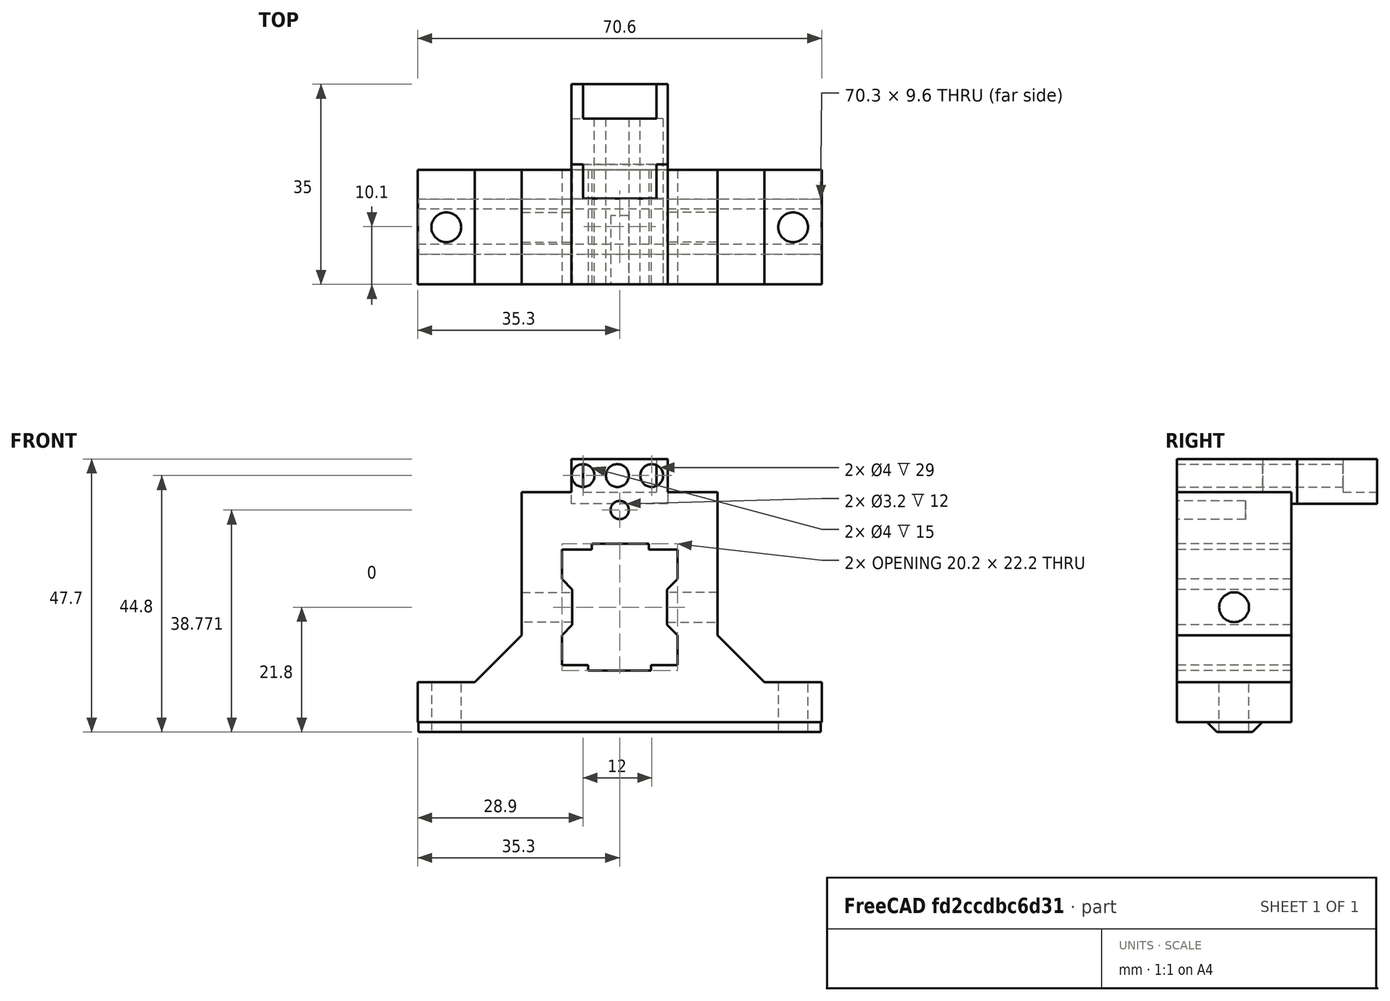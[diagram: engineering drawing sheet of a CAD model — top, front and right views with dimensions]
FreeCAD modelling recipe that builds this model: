
FCSTD DOCUMENT  (FreeCAD 1.0R39109 (Git))
Label: plotter_brace_limit_switch
License: All rights reserved
LicenseURL: https://en.wikipedia.org/wiki/All_rights_reserved
objects: Sketcher::SketchObject×24, PartDesign::Pocket×16, PartDesign::Pad×8, PartDesign::LinearPattern×2, PartDesign::Body×2, Mesh::Feature×1
note: 126 computed .brp shape members not serialized (recipe doc carries the construction recipe); baked Part::Feature solids carry a one-line shape summary decoded from their .brp

FEATURE [Mesh::Feature] _0x20_v_slot  label="20x20_v-slot"
FEATURE [Sketcher::SketchObject] Sketch
  ArcFitTolerance = 1e-06
  AttachmentSupport = -> [XZ_Plane]
  FullyConstrained = false
  MakeInternals = false
  MapMode = 5
  Placement = pos=(0,0,0) rot=(1,0,0;1.5708rad)
  sketch-geometry (28):
    g0: LineSegment StartX=-10.1 StartY=10.1 StartZ=0 EndX=-10.1 EndY=4.90001 EndZ=0
    g1: LineSegment StartX=-10.1 StartY=4.90001 StartZ=0 EndX=-8.3 EndY=3.09999 EndZ=0
    g2: LineSegment StartX=-8.3 StartY=3.09999 StartZ=0 EndX=-8.3 EndY=-3.10001 EndZ=0
    g3: LineSegment StartX=-8.3 StartY=-3.10001 StartZ=0 EndX=-10.1 EndY=-4.89999 EndZ=0
    g4: LineSegment StartX=-10.1 StartY=-4.89999 StartZ=0 EndX=-10.1 EndY=-10.1 EndZ=0
    g5: LineSegment StartX=-10.1 StartY=-10.1 StartZ=0 EndX=-5.47893 EndY=-10.1 EndZ=0
    g6: LineSegment StartX=-5.47893 StartY=-10.1 StartZ=0 EndX=-5.47893 EndY=-11.1 EndZ=0
    g7: LineSegment StartX=-5.47893 StartY=-11.1 StartZ=0 EndX=5.47893 EndY=-11.1 EndZ=0
    g8: LineSegment StartX=5.47893 StartY=-11.1 StartZ=0 EndX=5.47893 EndY=-10.1 EndZ=0
    g9: LineSegment StartX=5.47893 StartY=-10.1 StartZ=0 EndX=10.1 EndY=-10.1 EndZ=0
    g10: LineSegment StartX=10.1 StartY=-10.1 StartZ=0 EndX=10.1 EndY=-4.89999 EndZ=0
    g11: LineSegment StartX=10.1 StartY=-4.89999 StartZ=0 EndX=8.3 EndY=-3.09999 EndZ=0
    g12: LineSegment StartX=8.3 StartY=-3.09999 StartZ=0 EndX=8.3 EndY=3.10001 EndZ=0
    g13: LineSegment StartX=8.3 StartY=3.10001 StartZ=0 EndX=10.1 EndY=4.90001 EndZ=0
    g14: LineSegment StartX=10.1 StartY=4.90001 StartZ=0 EndX=10.1 EndY=10.1 EndZ=0
    g15: LineSegment StartX=17.1 StartY=10.1 StartZ=0 EndX=17.1 EndY=-4.89999 EndZ=0
    g16: LineSegment StartX=17.1 StartY=-4.89999 StartZ=0 EndX=25.3 EndY=-13.1 EndZ=0
    g17: LineSegment StartX=25.3 StartY=-13.1 StartZ=0 EndX=35.3 EndY=-13.1 EndZ=0
    g18: LineSegment StartX=35.3 StartY=-13.1 StartZ=0 EndX=35.3 EndY=-20.1 EndZ=0
    g19: LineSegment StartX=35.3 StartY=-20.1 StartZ=0 EndX=-35.3 EndY=-20.1 EndZ=0
    g20: LineSegment StartX=-35.3 StartY=-20.1 StartZ=0 EndX=-35.3 EndY=-13.1 EndZ=0
    g21: LineSegment StartX=-35.3 StartY=-13.1 StartZ=0 EndX=-25.3 EndY=-13.1 EndZ=0
    g22: LineSegment StartX=-25.3 StartY=-13.1 StartZ=0 EndX=-17.1 EndY=-4.89999 EndZ=0
    g23: LineSegment StartX=-17.1 StartY=-4.89999 StartZ=0 EndX=-17.1 EndY=10.1 EndZ=0
    g24: LineSegment StartX=-17.1 StartY=10.1 StartZ=0 EndX=-17.1 EndY=20.1 EndZ=0
    g25: LineSegment StartX=-17.1 StartY=20.1 StartZ=0 EndX=17.1 EndY=20.1 EndZ=0
    g26: LineSegment StartX=17.1 StartY=20.1 StartZ=0 EndX=17.1 EndY=10.1 EndZ=0
    g27: LineSegment StartX=10.1 StartY=10.1 StartZ=0 EndX=-10.1 EndY=10.1 EndZ=0
  constraints (81):
    c: Vertical(g0)
    c: Coincident(g0,g1)
    c: Coincident(g1,g2)
    c: Vertical(g2)
    c: Coincident(g2,g3)
    c: Coincident(g3,g4)
    c: Vertical(g4)
    c: Coincident(g4,g5)
    c: Horizontal(g5)
    c: Coincident(g5,g6)
    c: Vertical(g6)
    c: Coincident(g6,g7)
    c: Horizontal(g7)
    c: Coincident(g7,g8)
    c: Vertical(g8)
    c: Coincident(g8,g9)
    c: Horizontal(g9)
    c: Coincident(g9,g10)
    c: Vertical(g10)
    c: Coincident(g10,g11)
    c: Coincident(g11,g12)
    c: Vertical(g12)
    c: Coincident(g12,g13)
    c: Coincident(g13,g14)
    c: Vertical(g14)
    c: Vertical(g15)
    c: Coincident(g15,g16)
    c: Coincident(g16,g17)
    c: Horizontal(g17)
    c: Coincident(g17,g18)
    c: Vertical(g18)
    c: Coincident(g18,g19)
    c: Coincident(g19,g20)
    c: Vertical(g20)
    c: Coincident(g20,g21)
    c: Horizontal(g21)
    c: Coincident(g21,g22)
    c: Coincident(g22,g23)
    c: Vertical(g23)
    c: Equal(g15,g23)
    c: Equal(g14,g0)
    c: Equal(g12,g2)
    c: Equal(g4,g10)
    c: Equal(g9,g5)
    c: Equal(g6,g8)
    c: DistanceY(g8,g8) = 1
    c: DistanceY(g18,g18) = 7
    c: Equal(g20,g18)
    c: Equal(g21,g17)
    c: Symmetric(g18,g19,g-2)
    c: DistanceX(g4,g9) = 20.2
    c: DistanceX(g0,g14) = 20.2
    c: Perpendicular(g3,g1)
    c: Perpendicular(g11,g13)
    c: DistanceY(g2,g2) = 6.2
    c: DistanceX(g3,g2) = 1.8
    c: DistanceX(g11,g10) = 1.8
    c: DistanceY(g9,g14) = 20.2
    c: DistanceY(g14,g0) = 0
    c: DistanceX(g17,g17) = 10
    c: DistanceX(g14,g15) = 7
    c: Equal(g10,g14)
    c: Equal(g13,g11)
    c: Equal(g16,g22)
    c: Symmetric(g12,g2,g-1)
    c: DistanceY(g18,g9) = 10
    c: Perpendicular(g16,g22)
    c: DistanceY(g15,g10) = 0
    c: DistanceX(g23,g0) = 7
    c: Coincident(g23,g24)
    c: Vertical(g24)
    c: Coincident(g24,g25)
    c: Horizontal(g25)
    c: Coincident(g25,g26)
    c: Coincident(g26,g15)
    c: Vertical(g26)
    c: Coincident(g14,g27)
    c: Coincident(g27,g0)
    c: Equal(g24,g26)
    c: DistanceY(g26,g26) = 10
    c: DistanceY(g14,g15) = 0
FEATURE [PartDesign::Pad] Pad
  Direction = (0,-1,2e-16)
  Length = 20
  Length2 = 10
  Placement = pos=(0,0,0) rot=(1,0,0;1.5708rad)
  Profile = -> Sketch
  ReferenceAxis = -> Sketch [N_Axis]
  Refine = true
  Suppressed = false
  Type = 0
FEATURE [Sketcher::SketchObject] Sketch001
  ArcFitTolerance = 1e-06
  AttachmentSupport = -> [Pad]
  FullyConstrained = true
  MakeInternals = false
  MapMode = 5
  Placement = pos=(8.3,0,0) rot=(0.707107,0,-0.707107;3.14159rad)
  sketch-geometry (1):
    g0: Circle CenterX=0 CenterY=10 CenterZ=0 NormalX=0 NormalY=0 NormalZ=1 AngleXU=0 Radius=2.6
  constraints (4):
    c: Diameter(g0) = 5.2
    c: PointOnObject(g0,g-2)
    c: DistanceY(g-1,g0) = 10
    c: DistanceY(g-3,g-3) = 20
FEATURE [PartDesign::Pocket] Pocket
  BaseFeature = -> Pad
  Direction = (1,0,2e-16)
  Length = 100
  Length2 = 5
  Placement = pos=(0,0,0) rot=(1,0,0;1.5708rad)
  Profile = -> Sketch001
  ReferenceAxis = -> Sketch001 [N_Axis]
  Refine = true
  Suppressed = false
  Type = 0
FEATURE [PartDesign::Pocket] Pocket001
  BaseFeature = -> Pocket
  Direction = (1,0,2e-16)
  Length = 40
  Length2 = 5
  Placement = pos=(0,0,0) rot=(1,0,0;1.5708rad)
  Profile = -> Sketch001
  ReferenceAxis = -> Sketch001 [N_Axis]
  Refine = true
  Reversed = true
  Suppressed = false
  Type = 0
FEATURE [Sketcher::SketchObject] Sketch002
  ArcFitTolerance = 1e-06
  FullyConstrained = true
  MakeInternals = false
  MapMode = 5
  Placement = pos=(0,-20,0) rot=(1,0,0;1.5708rad)
  sketch-geometry (4):
    g0: LineSegment StartX=-10.05 StartY=4.89999 StartZ=0 EndX=-10.05 EndY=-4.90001 EndZ=0
    g1: LineSegment StartX=-10.05 StartY=-4.90001 StartZ=0 EndX=-8.25 EndY=-3.09999 EndZ=0
    g2: LineSegment StartX=-8.25 StartY=-3.09999 StartZ=0 EndX=-8.25 EndY=3.10001 EndZ=0
    g3: LineSegment StartX=-8.25 StartY=3.10001 StartZ=0 EndX=-10.05 EndY=4.89999 EndZ=0
  constraints (8):
    c: Coincident(g-3,g0)
    c: Coincident(g0,g-5)
    c: Coincident(g0,g1)
    c: Coincident(g1,g-5)
    c: Coincident(g1,g2)
    c: Coincident(g2,g-4)
    c: Coincident(g2,g3)
    c: Coincident(g3,g0)
FEATURE [Sketcher::SketchObject] Sketch003
  ArcFitTolerance = 1e-06
  FullyConstrained = true
  MakeInternals = false
  MapMode = 5
  Placement = pos=(35.15,0,0) rot=(0.707107,0,0.707107;3.14159rad)
  sketch-geometry (5):
    g0: GeomPoint X=-20 Y=10 Z=0
    g1: LineSegment StartX=-20 StartY=14.8 StartZ=0 EndX=-20 EndY=5 EndZ=0
    g2: LineSegment StartX=-20 StartY=5 StartZ=0 EndX=-21.8 EndY=6.8 EndZ=0
    g3: LineSegment StartX=-21.8 StartY=6.8 StartZ=0 EndX=-21.8 EndY=13 EndZ=0
    g4: LineSegment StartX=-21.8 StartY=13 StartZ=0 EndX=-20 EndY=14.8 EndZ=0
  constraints (12):
    c: Symmetric(g-3,g-3,g0)
    c: Coincident(g1,g2)
    c: Coincident(g2,g3)
    c: Coincident(g3,g4)
    c: Coincident(g4,g1)
    c: Equal(g2,g4)
    c: Parallel(g1,g3)
    c: DistanceY(g3,g3) = 6.2
    c: DistanceY(g1,g1) = 9.8
    c: Perpendicular(g4,g2)
    c: PointOnObject(g1,g-3)
    c: Symmetric(g0,g-3,g1)
FEATURE [PartDesign::Pad] Pad001
  BaseFeature = -> Pocket001
  Direction = (1,-1e-16,-2e-16)
  Length = 70.3
  Length2 = 10
  Placement = pos=(0,0,0) rot=(1,0,0;1.5708rad)
  Profile = -> Sketch003
  ReferenceAxis = -> Sketch003 [N_Axis]
  Refine = true
  Reversed = true
  Suppressed = false
  Type = 0
FEATURE [Sketcher::SketchObject] Sketch004
  ArcFitTolerance = 1e-06
  AttachmentSupport = -> [Pad001]
  ExternalGeometry = -> [Pad001]
  FullyConstrained = true
  MakeInternals = false
  MapMode = 5
  Placement = pos=(0,-2.9e-15,-13.1) rot=(0,0,1;3.14159rad)
  sketch-geometry (1):
    g0: Circle CenterX=-30.3 CenterY=10 CenterZ=0 NormalX=0 NormalY=0 NormalZ=1 AngleXU=0 Radius=2.6
  constraints (2):
    c: Diameter(g0) = 5.2
    c: Symmetric(g-4,g-3,g0)
FEATURE [PartDesign::Pocket] Pocket002
  BaseFeature = -> Pad001
  Direction = (0,0,-1)
  Length = 10
  Length2 = 5
  Placement = pos=(0,0,0) rot=(1,0,0;1.5708rad)
  Profile = -> Sketch004
  ReferenceAxis = -> Sketch004 [N_Axis]
  Refine = true
  Suppressed = false
  Type = 0
FEATURE [Sketcher::SketchObject] Sketch005
  ArcFitTolerance = 1e-06
  AttachmentSupport = -> [Pocket002]
  ExternalGeometry = -> [Pocket002]
  FullyConstrained = true
  MakeInternals = false
  MapMode = 5
  Placement = pos=(0,-2.9e-15,-13.1) rot=(0,0,1;3.14159rad)
  sketch-geometry (1):
    g0: Circle CenterX=30.3 CenterY=10 CenterZ=0 NormalX=0 NormalY=0 NormalZ=1 AngleXU=0 Radius=2.6
  constraints (2):
    c: Diameter(g0) = 5.2
    c: Symmetric(g-4,g-3,g0)
FEATURE [PartDesign::Pocket] Pocket003
  BaseFeature = -> Pocket002
  Direction = (0,0,-1)
  Length = 10
  Length2 = 5
  Placement = pos=(0,0,0) rot=(1,0,0;1.5708rad)
  Profile = -> Sketch005
  ReferenceAxis = -> Sketch005 [N_Axis]
  Refine = true
  Suppressed = false
  Type = 0
FEATURE [Sketcher::SketchObject] Sketch006
  ArcFitTolerance = 1e-06
  AttachmentSupport = -> [Pocket003]
  ExternalGeometry = -> [Pocket003]
  FullyConstrained = true
  MakeInternals = false
  MapMode = 5
  Placement = pos=(0,-8e-16,0) rot=(-1,0,0;1.5708rad)
  sketch-geometry (4):
    g0: LineSegment StartX=-4.9 StartY=-10.1 StartZ=0 EndX=-4.9 EndY=-11.1 EndZ=0
    g1: LineSegment StartX=-4.9 StartY=-11.1 StartZ=0 EndX=5.1 EndY=-11.1 EndZ=0
    g2: LineSegment StartX=5.1 StartY=-11.1 StartZ=0 EndX=5.1 EndY=-10.1 EndZ=0
    g3: LineSegment StartX=5.1 StartY=-10.1 StartZ=0 EndX=-4.9 EndY=-10.1 EndZ=0
  constraints (12):
    c: Coincident(g0,g1)
    c: Coincident(g1,g2)
    c: Coincident(g2,g3)
    c: Coincident(g3,g0)
    c: Vertical(g0)
    c: Vertical(g2)
    c: Horizontal(g1)
    c: Horizontal(g3)
    c: Distance(g0,g2) = 10
    c: Distance(g1,g3) = 1
    c: PointOnObject(g0,g-3)
    c: DistanceX(g2,g-3) = 5
FEATURE [PartDesign::Pocket] Pocket004
  BaseFeature = -> Pocket003
  Direction = (0,-1,-2e-16)
  Length = 25
  Length2 = 5
  Placement = pos=(0,0,0) rot=(1,0,0;1.5708rad)
  Profile = -> Sketch006
  ReferenceAxis = -> Sketch006 [N_Axis]
  Refine = true
  Suppressed = false
  Type = 0
FEATURE [Sketcher::SketchObject] Sketch007
  ArcFitTolerance = 1e-06
  AttachmentSupport = -> [Pocket004]
  ExternalGeometry = -> [Pocket004]
  FullyConstrained = false
  MakeInternals = false
  MapMode = 5
  Placement = pos=(0,4.5e-15,20.1) rot=(0,0,1;3.14159rad)
  sketch-geometry (7):
    g0: GeomPoint X=0 Y=20 Z=0
    g1: GeomPoint X=0 Y=0 Z=0
    g2: LineSegment StartX=-8.4 StartY=-15 StartZ=0 EndX=8.4 EndY=-15 EndZ=0
    g3: LineSegment StartX=8.4 StartY=-15 StartZ=0 EndX=8.4 EndY=20 EndZ=0
    g4: LineSegment StartX=8.4 StartY=20 StartZ=0 EndX=-8.4 EndY=20 EndZ=0
    g5: LineSegment StartX=-8.4 StartY=20 StartZ=0 EndX=-8.4 EndY=-15 EndZ=0
    g6: GeomPoint [constr] X=0 Y=2.5 Z=0
  constraints (14):
    c: Symmetric(g-3,g-3,g0)
    c: Coincident(g2,g3)
    c: Coincident(g3,g4)
    c: Coincident(g4,g5)
    c: Coincident(g5,g2)
    c: Horizontal(g2)
    c: Horizontal(g4)
    c: Vertical(g3)
    c: Vertical(g5)
    c: Symmetric(g4,g2,g6)
    c: Distance(g3,g5) = 16.8
    c: Distance(g2,g4) = 35
    c: PointOnObject(g6,g-2)
    c: PointOnObject(g3,g-3)
FEATURE [PartDesign::Pad] Pad002
  BaseFeature = -> Pocket004
  Direction = (0,0,1)
  Length = 5.8
  Length2 = 10
  Placement = pos=(0,0,0) rot=(1,0,0;1.5708rad)
  Profile = -> Sketch007
  ReferenceAxis = -> Sketch007 [N_Axis]
  Refine = true
  Suppressed = false
  Type = 0
FEATURE [Sketcher::SketchObject] Sketch008
  ArcFitTolerance = 1e-06
  AttachmentSupport = -> [Pad002]
  ExternalGeometry = -> [Pad002]
  FullyConstrained = true
  MakeInternals = false
  MapMode = 5
  Placement = pos=(0,0,25.9) rot=(0,0,1;3.14159rad)
  sketch-geometry (6):
    g0: LineSegment [constr] StartX=-8.4 StartY=-15 StartZ=0 EndX=-6.4 EndY=-15 EndZ=0
    g1: LineSegment StartX=-6.4 StartY=-15 StartZ=0 EndX=-6.4 EndY=-9 EndZ=0
    g2: LineSegment StartX=-6.4 StartY=-9 StartZ=0 EndX=6.4 EndY=-9 EndZ=0
    g3: LineSegment StartX=6.4 StartY=-9 StartZ=0 EndX=6.4 EndY=-15 EndZ=0
    g4: LineSegment [constr] StartX=6.4 StartY=-15 StartZ=0 EndX=8.4 EndY=-15 EndZ=0
    g5: LineSegment StartX=-6.4 StartY=-15 StartZ=0 EndX=6.4 EndY=-15 EndZ=0
  constraints (16):
    c: Coincident(g-3,g0)
    c: PointOnObject(g0,g-3)
    c: Coincident(g0,g1)
    c: Vertical(g1)
    c: Coincident(g1,g2)
    c: Horizontal(g2)
    c: Coincident(g2,g3)
    c: PointOnObject(g3,g-3)
    c: Vertical(g3)
    c: Coincident(g3,g4)
    c: Coincident(g4,g-3)
    c: Equal(g4,g0)
    c: DistanceX(g0,g0) = 2
    c: DistanceY(g3,g3) = 6
    c: Coincident(g5,g0)
    c: Coincident(g5,g3)
FEATURE [PartDesign::Pocket] Pocket005
  BaseFeature = -> Pad002
  Direction = (0,0,-1)
  Length = 5.8
  Length2 = 5
  Placement = pos=(0,0,0) rot=(1,0,0;1.5708rad)
  Profile = -> Sketch008
  ReferenceAxis = -> Sketch008 [N_Axis]
  Refine = true
  Suppressed = false
  Type = 0
FEATURE [Sketcher::SketchObject] Sketch009
  ArcFitTolerance = 1e-06
  AttachmentSupport = -> [Pocket005]
  ExternalGeometry = -> [Pocket005]
  FullyConstrained = true
  MakeInternals = false
  MapMode = 5
  Placement = pos=(0,-8e-16,0) rot=(-1,0,0;1.5708rad)
  sketch-geometry (4):
    g0: LineSegment StartX=-8.4 StartY=-20.1 StartZ=0 EndX=8.4 EndY=-20.1 EndZ=0
    g1: LineSegment StartX=8.4 StartY=-20.1 StartZ=0 EndX=8.4 EndY=-18.1 EndZ=0
    g2: LineSegment StartX=8.4 StartY=-18.1 StartZ=0 EndX=-8.4 EndY=-18.1 EndZ=0
    g3: LineSegment StartX=-8.4 StartY=-18.1 StartZ=0 EndX=-8.4 EndY=-20.1 EndZ=0
  constraints (11):
    c: Coincident(g0,g1)
    c: Coincident(g1,g2)
    c: Coincident(g2,g3)
    c: Coincident(g3,g0)
    c: Horizontal(g0)
    c: Horizontal(g2)
    c: Vertical(g1)
    c: Vertical(g3)
    c: Distance(g1,g3) = 16.8
    c: Distance(g0,g2) = 2
    c: Coincident(g0,g-3)
FEATURE [PartDesign::Pad] Pad003
  BaseFeature = -> Pocket005
  Direction = (0,1,2e-16)
  Length = 15
  Length2 = 10
  Placement = pos=(0,0,0) rot=(1,0,0;1.5708rad)
  Profile = -> Sketch009
  ReferenceAxis = -> Sketch009 [N_Axis]
  Refine = true
  Suppressed = false
  Type = 0
FEATURE [Sketcher::SketchObject] Sketch010
  ArcFitTolerance = 1e-06
  AttachmentSupport = -> [Pad003]
  ExternalGeometry = -> [Pad003]
  FullyConstrained = true
  MakeInternals = false
  MapMode = 5
  Placement = pos=(0,9,0) rot=(-1,0,0;1.5708rad)
  sketch-geometry (1):
    g0: Circle CenterX=-6.4 CenterY=-23 CenterZ=0 NormalX=0 NormalY=0 NormalZ=1 AngleXU=0 Radius=2
  constraints (2):
    c: Diameter(g0) = 4
    c: Symmetric(g-5,g-5,g0)
FEATURE [PartDesign::Pocket] Pocket006
  BaseFeature = -> Pad003
  Direction = (0,-1,-2e-16)
  Length = 40
  Length2 = 5
  Placement = pos=(0,0,0) rot=(1,0,0;1.5708rad)
  Profile = -> Sketch010
  ReferenceAxis = -> Sketch010 [N_Axis]
  Refine = true
  Suppressed = false
  Type = 0
FEATURE [PartDesign::LinearPattern] LinearPattern
  BaseFeature = -> Pocket006
  Direction = -> Sketch010 [H_Axis]
  Length = 12
  Mode = 0
  Occurrences = 3
  Offset = 6
  Originals = -> [Pocket006]
  Placement = pos=(0,0,0) rot=(1,0,0;1.5708rad)
  Refine = true
  Suppressed = false
  TransformMode = 0
FEATURE [Sketcher::SketchObject] Sketch011
  ArcFitTolerance = 1e-06
  AttachmentSupport = -> [LinearPattern]
  FullyConstrained = false
  MakeInternals = false
  MapMode = 5
  Placement = pos=(0,-20,4.4e-15) rot=(1,0,0;1.5708rad)
  sketch-geometry (1):
    g0: Circle CenterX=0 CenterY=16.9706 CenterZ=0 NormalX=0 NormalY=0 NormalZ=1 AngleXU=0 Radius=1.6
  constraints (2):
    c: Diameter(g0) = 3.2
    c: PointOnObject(g0,g-2)
FEATURE [PartDesign::Pocket] Pocket007
  BaseFeature = -> LinearPattern
  Direction = (0,1,-2e-16)
  Length = 12
  Length2 = 5
  Placement = pos=(0,0,0) rot=(1,0,0;1.5708rad)
  Profile = -> Sketch011
  ReferenceAxis = -> Sketch011 [N_Axis]
  Refine = true
  Suppressed = false
  Type = 0
FEATURE [PartDesign::Body] Body  label="main"
  AllowCompound = false
  Group = -> [Sketch,Pad,Sketch001,Pocket,Pocket001,Sketch002,Sketch003,Pad001,Sketch004,Pocket002,Sketch005,Pocket003,Sketch006,Pocket004,Sketch007,Pad002,Sketch008,Pocket005,Sketch009,Pad003,Sketch010,Pocket006,LinearPattern,Sketch011,Pocket007]
  Origin = -> Origin
  Tip = -> Pocket007
FEATURE [Sketcher::SketchObject] Sketch012
  ArcFitTolerance = 1e-06
  AttachmentSupport = -> [XZ_Plane001]
  FullyConstrained = false
  MakeInternals = false
  MapMode = 5
  Placement = pos=(0,0,0) rot=(1,0,0;1.5708rad)
  sketch-geometry (28):
    g0: LineSegment StartX=-10.1 StartY=10.1 StartZ=0 EndX=-10.1 EndY=4.90001 EndZ=0
    g1: LineSegment StartX=-10.1 StartY=4.90001 StartZ=0 EndX=-8.3 EndY=3.09999 EndZ=0
    g2: LineSegment StartX=-8.3 StartY=3.09999 StartZ=0 EndX=-8.3 EndY=-3.10001 EndZ=0
    g3: LineSegment StartX=-8.3 StartY=-3.10001 StartZ=0 EndX=-10.1 EndY=-4.89999 EndZ=0
    g4: LineSegment StartX=-10.1 StartY=-4.89999 StartZ=0 EndX=-10.1 EndY=-10.1 EndZ=0
    g5: LineSegment StartX=-10.1 StartY=-10.1 StartZ=0 EndX=-5.47893 EndY=-10.1 EndZ=0
    g6: LineSegment StartX=-5.47893 StartY=-10.1 StartZ=0 EndX=-5.47893 EndY=-11.1 EndZ=0
    g7: LineSegment StartX=-5.47893 StartY=-11.1 StartZ=0 EndX=5.47893 EndY=-11.1 EndZ=0
    g8: LineSegment StartX=5.47893 StartY=-11.1 StartZ=0 EndX=5.47893 EndY=-10.1 EndZ=0
    g9: LineSegment StartX=5.47893 StartY=-10.1 StartZ=0 EndX=10.1 EndY=-10.1 EndZ=0
    g10: LineSegment StartX=10.1 StartY=-10.1 StartZ=0 EndX=10.1 EndY=-4.89999 EndZ=0
    g11: LineSegment StartX=10.1 StartY=-4.89999 StartZ=0 EndX=8.3 EndY=-3.09999 EndZ=0
    g12: LineSegment StartX=8.3 StartY=-3.09999 StartZ=0 EndX=8.3 EndY=3.10001 EndZ=0
    g13: LineSegment StartX=8.3 StartY=3.10001 StartZ=0 EndX=10.1 EndY=4.90001 EndZ=0
    g14: LineSegment StartX=10.1 StartY=4.90001 StartZ=0 EndX=10.1 EndY=10.1 EndZ=0
    g15: LineSegment StartX=17.1 StartY=10.1 StartZ=0 EndX=17.1 EndY=-4.89999 EndZ=0
    g16: LineSegment StartX=17.1 StartY=-4.89999 StartZ=0 EndX=25.3 EndY=-13.1 EndZ=0
    g17: LineSegment StartX=25.3 StartY=-13.1 StartZ=0 EndX=35.3 EndY=-13.1 EndZ=0
    g18: LineSegment StartX=35.3 StartY=-13.1 StartZ=0 EndX=35.3 EndY=-20.1 EndZ=0
    g19: LineSegment StartX=35.3 StartY=-20.1 StartZ=0 EndX=-35.3 EndY=-20.1 EndZ=0
    g20: LineSegment StartX=-35.3 StartY=-20.1 StartZ=0 EndX=-35.3 EndY=-13.1 EndZ=0
    g21: LineSegment StartX=-35.3 StartY=-13.1 StartZ=0 EndX=-25.3 EndY=-13.1 EndZ=0
    g22: LineSegment StartX=-25.3 StartY=-13.1 StartZ=0 EndX=-17.1 EndY=-4.89999 EndZ=0
    g23: LineSegment StartX=-17.1 StartY=-4.89999 StartZ=0 EndX=-17.1 EndY=10.1 EndZ=0
    g24: LineSegment StartX=-17.1 StartY=10.1 StartZ=0 EndX=-17.1 EndY=20.1 EndZ=0
    g25: LineSegment StartX=-17.1 StartY=20.1 StartZ=0 EndX=17.1 EndY=20.1 EndZ=0
    g26: LineSegment StartX=17.1 StartY=20.1 StartZ=0 EndX=17.1 EndY=10.1 EndZ=0
    g27: LineSegment StartX=10.1 StartY=10.1 StartZ=0 EndX=-10.1 EndY=10.1 EndZ=0
  constraints (81):
    c: Vertical(g0)
    c: Coincident(g0,g1)
    c: Coincident(g1,g2)
    c: Vertical(g2)
    c: Coincident(g2,g3)
    c: Coincident(g3,g4)
    c: Vertical(g4)
    c: Coincident(g4,g5)
    c: Horizontal(g5)
    c: Coincident(g5,g6)
    c: Vertical(g6)
    c: Coincident(g6,g7)
    c: Horizontal(g7)
    c: Coincident(g7,g8)
    c: Vertical(g8)
    c: Coincident(g8,g9)
    c: Horizontal(g9)
    c: Coincident(g9,g10)
    c: Vertical(g10)
    c: Coincident(g10,g11)
    c: Coincident(g11,g12)
    c: Vertical(g12)
    c: Coincident(g12,g13)
    c: Coincident(g13,g14)
    c: Vertical(g14)
    c: Vertical(g15)
    c: Coincident(g15,g16)
    c: Coincident(g16,g17)
    c: Horizontal(g17)
    c: Coincident(g17,g18)
    c: Vertical(g18)
    c: Coincident(g18,g19)
    c: Coincident(g19,g20)
    c: Vertical(g20)
    c: Coincident(g20,g21)
    c: Horizontal(g21)
    c: Coincident(g21,g22)
    c: Coincident(g22,g23)
    c: Vertical(g23)
    c: Equal(g15,g23)
    c: Equal(g14,g0)
    c: Equal(g12,g2)
    c: Equal(g4,g10)
    c: Equal(g9,g5)
    c: Equal(g6,g8)
    c: DistanceY(g8,g8) = 1
    c: DistanceY(g18,g18) = 7
    c: Equal(g20,g18)
    c: Equal(g21,g17)
    c: Symmetric(g18,g19,g-2)
    c: DistanceX(g4,g9) = 20.2
    c: DistanceX(g0,g14) = 20.2
    c: Perpendicular(g3,g1)
    c: Perpendicular(g11,g13)
    c: DistanceY(g2,g2) = 6.2
    c: DistanceX(g3,g2) = 1.8
    c: DistanceX(g11,g10) = 1.8
    c: DistanceY(g9,g14) = 20.2
    c: DistanceY(g14,g0) = 0
    c: DistanceX(g17,g17) = 10
    c: DistanceX(g14,g15) = 7
    c: Equal(g10,g14)
    c: Equal(g13,g11)
    c: Equal(g16,g22)
    c: Symmetric(g12,g2,g-1)
    c: DistanceY(g18,g9) = 10
    c: Perpendicular(g16,g22)
    c: DistanceY(g15,g10) = 0
    c: DistanceX(g23,g0) = 7
    c: Coincident(g23,g24)
    c: Vertical(g24)
    c: Coincident(g24,g25)
    c: Horizontal(g25)
    c: Coincident(g25,g26)
    c: Coincident(g26,g15)
    c: Vertical(g26)
    c: Coincident(g14,g27)
    c: Coincident(g27,g0)
    c: Equal(g24,g26)
    c: DistanceY(g26,g26) = 10
    c: DistanceY(g14,g15) = 0
FEATURE [PartDesign::Pad] Pad004
  Direction = (0,-1,2e-16)
  Length = 20
  Length2 = 10
  Placement = pos=(0,0,0) rot=(1,0,0;1.5708rad)
  Profile = -> Sketch012
  ReferenceAxis = -> Sketch012 [N_Axis]
  Refine = true
  Suppressed = false
  Type = 0
FEATURE [Sketcher::SketchObject] Sketch013
  ArcFitTolerance = 1e-06
  AttachmentSupport = -> [Pad004]
  FullyConstrained = true
  MakeInternals = false
  MapMode = 5
  Placement = pos=(8.3,0,0) rot=(0.707107,0,-0.707107;3.14159rad)
  sketch-geometry (1):
    g0: Circle CenterX=0 CenterY=10 CenterZ=0 NormalX=0 NormalY=0 NormalZ=1 AngleXU=0 Radius=2.6
  constraints (4):
    c: Diameter(g0) = 5.2
    c: PointOnObject(g0,g-2)
    c: DistanceY(g-1,g0) = 10
    c: DistanceY(g-3,g-3) = 20
FEATURE [PartDesign::Pocket] Pocket008
  BaseFeature = -> Pad004
  Direction = (1,0,2e-16)
  Length = 100
  Length2 = 5
  Placement = pos=(0,0,0) rot=(1,0,0;1.5708rad)
  Profile = -> Sketch013
  ReferenceAxis = -> Sketch013 [N_Axis]
  Refine = true
  Suppressed = false
  Type = 0
FEATURE [PartDesign::Pocket] Pocket009
  BaseFeature = -> Pocket008
  Direction = (1,0,2e-16)
  Length = 40
  Length2 = 5
  Placement = pos=(0,0,0) rot=(1,0,0;1.5708rad)
  Profile = -> Sketch013
  ReferenceAxis = -> Sketch013 [N_Axis]
  Refine = true
  Reversed = true
  Suppressed = false
  Type = 0
FEATURE [Sketcher::SketchObject] Sketch014
  ArcFitTolerance = 1e-06
  FullyConstrained = true
  MakeInternals = false
  MapMode = 5
  Placement = pos=(0,-20,0) rot=(1,0,0;1.5708rad)
  sketch-geometry (4):
    g0: LineSegment StartX=-10.05 StartY=4.89999 StartZ=0 EndX=-10.05 EndY=-4.90001 EndZ=0
    g1: LineSegment StartX=-10.05 StartY=-4.90001 StartZ=0 EndX=-8.25 EndY=-3.09999 EndZ=0
    g2: LineSegment StartX=-8.25 StartY=-3.09999 StartZ=0 EndX=-8.25 EndY=3.10001 EndZ=0
    g3: LineSegment StartX=-8.25 StartY=3.10001 StartZ=0 EndX=-10.05 EndY=4.89999 EndZ=0
  constraints (8):
    c: Coincident(g-3,g0)
    c: Coincident(g0,g-5)
    c: Coincident(g0,g1)
    c: Coincident(g1,g-5)
    c: Coincident(g1,g2)
    c: Coincident(g2,g-4)
    c: Coincident(g2,g3)
    c: Coincident(g3,g0)
FEATURE [Sketcher::SketchObject] Sketch015
  ArcFitTolerance = 1e-06
  FullyConstrained = true
  MakeInternals = false
  MapMode = 5
  Placement = pos=(35.15,0,0) rot=(0.707107,0,0.707107;3.14159rad)
  sketch-geometry (5):
    g0: GeomPoint X=-20 Y=10 Z=0
    g1: LineSegment StartX=-20 StartY=14.8 StartZ=0 EndX=-20 EndY=5 EndZ=0
    g2: LineSegment StartX=-20 StartY=5 StartZ=0 EndX=-21.8 EndY=6.8 EndZ=0
    g3: LineSegment StartX=-21.8 StartY=6.8 StartZ=0 EndX=-21.8 EndY=13 EndZ=0
    g4: LineSegment StartX=-21.8 StartY=13 StartZ=0 EndX=-20 EndY=14.8 EndZ=0
  constraints (12):
    c: Symmetric(g-3,g-3,g0)
    c: Coincident(g1,g2)
    c: Coincident(g2,g3)
    c: Coincident(g3,g4)
    c: Coincident(g4,g1)
    c: Equal(g2,g4)
    c: Parallel(g1,g3)
    c: DistanceY(g3,g3) = 6.2
    c: DistanceY(g1,g1) = 9.8
    c: Perpendicular(g4,g2)
    c: PointOnObject(g1,g-3)
    c: Symmetric(g0,g-3,g1)
FEATURE [PartDesign::Pad] Pad005
  BaseFeature = -> Pocket009
  Direction = (1,-1e-16,-2e-16)
  Length = 70.3
  Length2 = 10
  Placement = pos=(0,0,0) rot=(1,0,0;1.5708rad)
  Profile = -> Sketch015
  ReferenceAxis = -> Sketch015 [N_Axis]
  Refine = true
  Reversed = true
  Suppressed = false
  Type = 0
FEATURE [Sketcher::SketchObject] Sketch016
  ArcFitTolerance = 1e-06
  AttachmentSupport = -> [Pad005]
  ExternalGeometry = -> [Pad005]
  FullyConstrained = true
  MakeInternals = false
  MapMode = 5
  Placement = pos=(0,-2.9e-15,-13.1) rot=(0,0,1;3.14159rad)
  sketch-geometry (1):
    g0: Circle CenterX=-30.3 CenterY=10 CenterZ=0 NormalX=0 NormalY=0 NormalZ=1 AngleXU=0 Radius=2.6
  constraints (2):
    c: Diameter(g0) = 5.2
    c: Symmetric(g-4,g-3,g0)
FEATURE [PartDesign::Pocket] Pocket010
  BaseFeature = -> Pad005
  Direction = (0,0,-1)
  Length = 10
  Length2 = 5
  Placement = pos=(0,0,0) rot=(1,0,0;1.5708rad)
  Profile = -> Sketch016
  ReferenceAxis = -> Sketch016 [N_Axis]
  Refine = true
  Suppressed = false
  Type = 0
FEATURE [Sketcher::SketchObject] Sketch017
  ArcFitTolerance = 1e-06
  AttachmentSupport = -> [Pocket010]
  ExternalGeometry = -> [Pocket010]
  FullyConstrained = true
  MakeInternals = false
  MapMode = 5
  Placement = pos=(0,-2.9e-15,-13.1) rot=(0,0,1;3.14159rad)
  sketch-geometry (1):
    g0: Circle CenterX=30.3 CenterY=10 CenterZ=0 NormalX=0 NormalY=0 NormalZ=1 AngleXU=0 Radius=2.6
  constraints (2):
    c: Diameter(g0) = 5.2
    c: Symmetric(g-4,g-3,g0)
FEATURE [PartDesign::Pocket] Pocket011
  BaseFeature = -> Pocket010
  Direction = (0,0,-1)
  Length = 10
  Length2 = 5
  Placement = pos=(0,0,0) rot=(1,0,0;1.5708rad)
  Profile = -> Sketch017
  ReferenceAxis = -> Sketch017 [N_Axis]
  Refine = true
  Suppressed = false
  Type = 0
FEATURE [Sketcher::SketchObject] Sketch018
  ArcFitTolerance = 1e-06
  AttachmentSupport = -> [Pocket011]
  ExternalGeometry = -> [Pocket011]
  FullyConstrained = true
  MakeInternals = false
  MapMode = 5
  Placement = pos=(0,-8e-16,0) rot=(-1,0,0;1.5708rad)
  sketch-geometry (4):
    g0: LineSegment StartX=-4.9 StartY=-10.1 StartZ=0 EndX=-4.9 EndY=-11.1 EndZ=0
    g1: LineSegment StartX=-4.9 StartY=-11.1 StartZ=0 EndX=5.1 EndY=-11.1 EndZ=0
    g2: LineSegment StartX=5.1 StartY=-11.1 StartZ=0 EndX=5.1 EndY=-10.1 EndZ=0
    g3: LineSegment StartX=5.1 StartY=-10.1 StartZ=0 EndX=-4.9 EndY=-10.1 EndZ=0
  constraints (12):
    c: Coincident(g0,g1)
    c: Coincident(g1,g2)
    c: Coincident(g2,g3)
    c: Coincident(g3,g0)
    c: Vertical(g0)
    c: Vertical(g2)
    c: Horizontal(g1)
    c: Horizontal(g3)
    c: Distance(g0,g2) = 10
    c: Distance(g1,g3) = 1
    c: PointOnObject(g0,g-3)
    c: DistanceX(g2,g-3) = 5
FEATURE [PartDesign::Pocket] Pocket012
  BaseFeature = -> Pocket011
  Direction = (0,-1,-2e-16)
  Length = 25
  Length2 = 5
  Placement = pos=(0,0,0) rot=(1,0,0;1.5708rad)
  Profile = -> Sketch018
  ReferenceAxis = -> Sketch018 [N_Axis]
  Refine = true
  Suppressed = false
  Type = 0
FEATURE [Sketcher::SketchObject] Sketch019
  ArcFitTolerance = 1e-06
  AttachmentSupport = -> [Pocket012]
  ExternalGeometry = -> [Pocket012]
  FullyConstrained = false
  MakeInternals = false
  MapMode = 5
  Placement = pos=(0,4.5e-15,20.1) rot=(0,0,1;3.14159rad)
  sketch-geometry (7):
    g0: GeomPoint X=0 Y=20 Z=0
    g1: GeomPoint X=0 Y=0 Z=0
    g2: LineSegment StartX=-8.4 StartY=-1 StartZ=0 EndX=8.4 EndY=-1 EndZ=0
    g3: LineSegment StartX=8.4 StartY=-1 StartZ=0 EndX=8.4 EndY=20 EndZ=0
    g4: LineSegment StartX=8.4 StartY=20 StartZ=0 EndX=-8.4 EndY=20 EndZ=0
    g5: LineSegment StartX=-8.4 StartY=20 StartZ=0 EndX=-8.4 EndY=-1 EndZ=0
    g6: GeomPoint [constr] X=0 Y=9.5 Z=0
  constraints (14):
    c: Symmetric(g-3,g-3,g0)
    c: Coincident(g2,g3)
    c: Coincident(g3,g4)
    c: Coincident(g4,g5)
    c: Coincident(g5,g2)
    c: Horizontal(g2)
    c: Horizontal(g4)
    c: Vertical(g3)
    c: Vertical(g5)
    c: Symmetric(g4,g2,g6)
    c: Distance(g3,g5) = 16.8
    c: Distance(g2,g4) = 21
    c: PointOnObject(g6,g-2)
    c: PointOnObject(g3,g-3)
FEATURE [PartDesign::Pad] Pad006
  BaseFeature = -> Pocket012
  Direction = (0,0,1)
  Length = 5.8
  Length2 = 10
  Placement = pos=(0,0,0) rot=(1,0,0;1.5708rad)
  Profile = -> Sketch019
  ReferenceAxis = -> Sketch019 [N_Axis]
  Refine = true
  Suppressed = false
  Type = 0
FEATURE [Sketcher::SketchObject] Sketch020
  ArcFitTolerance = 1e-06
  AttachmentSupport = -> [Pad006]
  ExternalGeometry = -> [Pad006]
  FullyConstrained = true
  MakeInternals = false
  MapMode = 5
  Placement = pos=(0,0,25.9) rot=(0,0,1;3.14159rad)
  sketch-geometry (6):
    g0: LineSegment [constr] StartX=-8.4 StartY=-1 StartZ=0 EndX=-6.4 EndY=-1 EndZ=0
    g1: LineSegment StartX=-6.4 StartY=-1 StartZ=0 EndX=-6.4 EndY=5 EndZ=0
    g2: LineSegment StartX=-6.4 StartY=5 StartZ=0 EndX=6.4 EndY=5 EndZ=0
    g3: LineSegment StartX=6.4 StartY=5 StartZ=0 EndX=6.4 EndY=-1 EndZ=0
    g4: LineSegment [constr] StartX=6.4 StartY=-1 StartZ=0 EndX=8.4 EndY=-1 EndZ=0
    g5: LineSegment StartX=-6.4 StartY=-1 StartZ=0 EndX=6.4 EndY=-1 EndZ=0
  constraints (16):
    c: Coincident(g-3,g0)
    c: PointOnObject(g0,g-3)
    c: Coincident(g0,g1)
    c: Vertical(g1)
    c: Coincident(g1,g2)
    c: Horizontal(g2)
    c: Coincident(g2,g3)
    c: PointOnObject(g3,g-3)
    c: Vertical(g3)
    c: Coincident(g3,g4)
    c: Coincident(g4,g-3)
    c: Equal(g4,g0)
    c: DistanceX(g0,g0) = 2
    c: DistanceY(g3,g3) = 6
    c: Coincident(g5,g0)
    c: Coincident(g5,g3)
FEATURE [PartDesign::Pocket] Pocket013
  BaseFeature = -> Pad006
  Direction = (0,0,-1)
  Length = 5.8
  Length2 = 5
  Placement = pos=(0,0,0) rot=(1,0,0;1.5708rad)
  Profile = -> Sketch020
  ReferenceAxis = -> Sketch020 [N_Axis]
  Refine = true
  Suppressed = false
  Type = 0
FEATURE [Sketcher::SketchObject] Sketch021
  ArcFitTolerance = 1e-06
  AttachmentSupport = -> [Pocket013]
  FullyConstrained = true
  MakeInternals = false
  MapMode = 5
  Placement = pos=(0,-8e-16,0) rot=(-1,0,0;1.5708rad)
  sketch-geometry (4):
    g0: LineSegment StartX=-8.4 StartY=-20.1 StartZ=0 EndX=8.4 EndY=-20.1 EndZ=0
    g1: LineSegment StartX=8.4 StartY=-20.1 StartZ=0 EndX=8.4 EndY=-18.1 EndZ=0
    g2: LineSegment StartX=8.4 StartY=-18.1 StartZ=0 EndX=-8.4 EndY=-18.1 EndZ=0
    g3: LineSegment StartX=-8.4 StartY=-18.1 StartZ=0 EndX=-8.4 EndY=-20.1 EndZ=0
  constraints (11):
    c: Coincident(g0,g1)
    c: Coincident(g1,g2)
    c: Coincident(g2,g3)
    c: Coincident(g3,g0)
    c: Horizontal(g0)
    c: Horizontal(g2)
    c: Vertical(g1)
    c: Vertical(g3)
    c: Distance(g1,g3) = 16.8
    c: Distance(g0,g2) = 2
    c: Coincident(g0,g-3)
FEATURE [PartDesign::Pad] Pad007
  BaseFeature = -> Pocket013
  Direction = (0,1,2e-16)
  Length = 1
  Length2 = 10
  Placement = pos=(0,0,0) rot=(1,0,0;1.5708rad)
  Profile = -> Sketch021
  ReferenceAxis = -> Sketch021 [N_Axis]
  Refine = true
  Suppressed = false
  Type = 0
FEATURE [Sketcher::SketchObject] Sketch022
  ArcFitTolerance = 1e-06
  AttachmentSupport = -> [Pad007]
  ExternalGeometry = -> [Pad007]
  FullyConstrained = true
  MakeInternals = false
  MapMode = 5
  Placement = pos=(0,-5,0) rot=(-1,0,0;1.5708rad)
  sketch-geometry (1):
    g0: Circle CenterX=-6.4 CenterY=-23 CenterZ=0 NormalX=0 NormalY=0 NormalZ=1 AngleXU=0 Radius=2
  constraints (2):
    c: Diameter(g0) = 4
    c: Symmetric(g-5,g-5,g0)
FEATURE [PartDesign::Pocket] Pocket014
  BaseFeature = -> Pad007
  Direction = (0,-1,-2e-16)
  Length = 40
  Length2 = 5
  Placement = pos=(0,0,0) rot=(1,0,0;1.5708rad)
  Profile = -> Sketch022
  ReferenceAxis = -> Sketch022 [N_Axis]
  Refine = true
  Suppressed = false
  Type = 0
FEATURE [PartDesign::LinearPattern] LinearPattern001
  BaseFeature = -> Pocket014
  Direction = -> Sketch022 [H_Axis]
  Length = 12
  Mode = 0
  Occurrences = 3
  Offset = 6
  Originals = -> [Pocket014]
  Placement = pos=(0,0,0) rot=(1,0,0;1.5708rad)
  Refine = true
  Suppressed = false
  TransformMode = 0
FEATURE [Sketcher::SketchObject] Sketch023
  ArcFitTolerance = 1e-06
  AttachmentSupport = -> [LinearPattern001]
  FullyConstrained = false
  MakeInternals = false
  MapMode = 5
  Placement = pos=(0,-20,5.1e-15) rot=(1,0,0;1.5708rad)
  sketch-geometry (1):
    g0: Circle CenterX=0 CenterY=16.9706 CenterZ=0 NormalX=0 NormalY=0 NormalZ=1 AngleXU=0 Radius=1.6
  constraints (2):
    c: Diameter(g0) = 3.2
    c: PointOnObject(g0,g-2)
FEATURE [PartDesign::Pocket] Pocket015
  BaseFeature = -> LinearPattern001
  Direction = (0,1,-2e-16)
  Length = 12
  Length2 = 5
  Placement = pos=(0,0,0) rot=(1,0,0;1.5708rad)
  Profile = -> Sketch023
  ReferenceAxis = -> Sketch023 [N_Axis]
  Refine = true
  Suppressed = false
  Type = 0
FEATURE [PartDesign::Body] Body001  label="front"
  AllowCompound = false
  Group = -> [Sketch012,Pad004,Sketch013,Pocket008,Pocket009,Sketch014,Sketch015,Pad005,Sketch016,Pocket010,Sketch017,Pocket011,Sketch018,Pocket012,Sketch019,Pad006,Sketch020,Pocket013,Sketch021,Pad007,Sketch022,Pocket014,LinearPattern001,Sketch023,Pocket015]
  Origin = -> Origin001
  Tip = -> Pocket015
